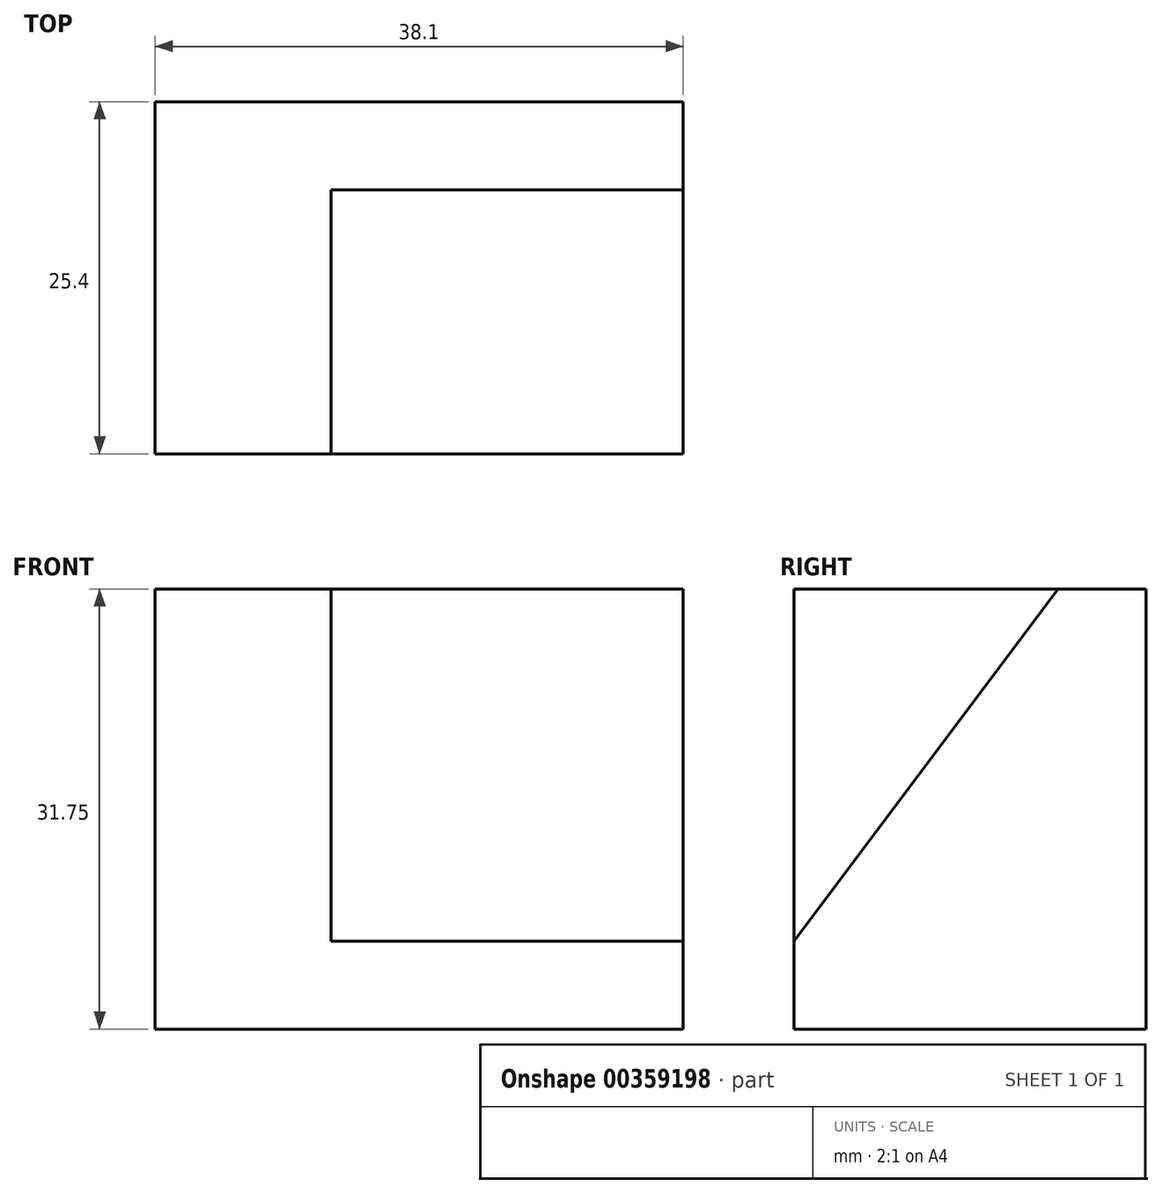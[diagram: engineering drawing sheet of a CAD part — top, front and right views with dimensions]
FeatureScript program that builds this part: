
annotation { "Feature Type Name" : "Feature", "Feature Type Description" : "" }
export const myFeature = defineFeature(function(context is Context, id is Id, definition is map)
    precondition{}
    {
        {
            var Q0;
            Q0=qCreatedBy(makeId("Front.planeOp"),FACE);
            var sketch = newSketch(context, id + "F0", { "sketchPlane" : qUnion([Q0])});
            skLineSegment(sketch, "E0", {"start": v(0, 0) * mm, "end": v(0, 31.75) * mm});
            skLineSegment(sketch, "E1", {"start": v(0, 31.75) * mm, "end": v(12.7, 31.75) * mm});
            skLineSegment(sketch, "E2", {"start": v(12.7, 31.75) * mm, "end": v(12.7, 6.35) * mm});
            skLineSegment(sketch, "E3", {"start": v(12.7, 6.35) * mm, "end": v(38.1, 6.35) * mm});
            skLineSegment(sketch, "E4", {"start": v(38.1, 6.35) * mm, "end": v(38.1, 0) * mm});
            skLineSegment(sketch, "E5", {"start": v(38.1, 0) * mm, "end": v(0, 0) * mm});
            skSolve(sketch);
        }
        {
            var Q0;
            Q0 = qSketchRegion(id + "F0", true);
            extrude(context, id + "F1", {"entities" : qUnion([Q0]), "oppositeDirection" : true, "depth" : 25.4 * mm});
        }
        {
            var Q0;
            Q0=makeQuery(id+"F1.opExtrude","SWEPT_FACE",FACE,{"disambiguationData":[OSD([sQuery(id+"F0.wireOp",EDGE,"E2")])]});
            var sketch = newSketch(context, id + "F2", { "sketchPlane" : qUnion([Q0])});
            skLineSegment(sketch, "E6", {"start": v(25.4, 31.75) * mm, "end": v(19.05, 31.75) * mm});
            skLineSegment(sketch, "E7", {"start": v(19.05, 31.75) * mm, "end": v(0, 6.35) * mm});
            skSolve(sketch);
        }
        {
            var Q0;
            Q0 = qSketchRegion(id + "F2", true);
            var Q1;
            Q1=makeQuery(id+"F2.imprint","IMPRINT",FACE,{"disambiguationData":[TD([[makeQuery(id+"F2.imprint","IMPRINT",EDGE,{"derivedFrom":sQuery(id+"F2.wireOp",EDGE,"E6")}),1.0]])]});
            extrude(context, id + "F3", {"entities" : qUnion([Q0, Q1]), "operationType" : NewBodyOperationType.ADD, "depth" : 25.4 * mm});
        }
    });
